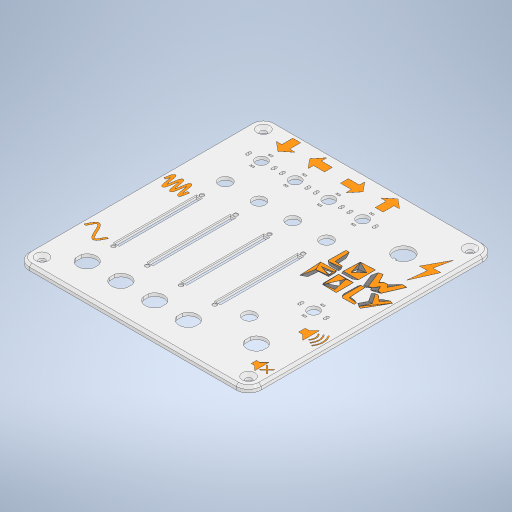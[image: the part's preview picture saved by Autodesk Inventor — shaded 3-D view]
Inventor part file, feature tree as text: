
AUTODESK INVENTOR PART (.ipt)
format: ipt  version: 2024.1 (Build 281209000, 209)  size: 8,079,360 bytes
history: native  units: mm
features: projected_geometry x59, sketch x58, extrude x57, fillet x24, other x13, chamfer x10, plane x2, pattern_linear x2
ambient origin geometry x8: Origin, YZ Plane, XZ Plane, XY Plane, X Axis, Y Axis, Z Axis, Center Point
bodies: Solid12 (feature_tree)
feature tree (225):
  other  "items"
  other  "Blocks"
  extrude  "Extrusion1"  Depth=9.5mm
  extrude  "Extrusion2"  Depth=9.5mm
  extrude  "Extrusion3"  Depth=12.0mm
  extrude  "Extrusion4"  Depth=12.0mm
  extrude  "Extrusion5"  Depth=3.3mm
  extrude  "Extrusion6"  Depth=4.0mm
  extrude  "Extrusion7"  Depth=3.3mm
  extrude  "Extrusion8"  Depth=3.3mm
  extrude  "Extrusion9"  Depth=3.3mm
  extrude  "Extrusion31"  Depth=4.3mm TaperAngle=0.0deg
  fillet  "Fillet1"  Radius=1.76mm
  extrude  "Extrusion10"  Depth=0.57mm
  plane  "Work Plane1"
  extrude  "Extrusion11"  Depth=4.96mm
  extrude  "Extrusion12"  Depth=1.22mm
  chamfer  "Chamfer1"  Distance=15.0mm
  extrude  "Extrusion13"  Depth=4.96mm
  fillet  "Fillet3"  Radius=0.49mm
  extrude  "Extrusion14"  Depth=5.0mm TaperAngle=0.0deg
  fillet  "Fillet4"  Radius=1.6mm
  extrude  "Extrusion15"  Depth=56.35mm
  extrude  "Extrusion16"  Depth=5.0mm TaperAngle=0.0deg
  extrude  "Extrusion17"  Depth=15.2mm
  extrude  "Extrusion21"  Depth=30.0mm
  extrude  "Extrusion30"  Depth=30.0mm
  fillet  "Fillet5"  Radius=10.35mm
  extrude  "Extrusion18"  Depth=1.2mm
  extrude  "Extrusion19"  Depth=7.5mm
  extrude  "Extrusion20"  Depth=5.9mm
  fillet  "Fillet6"  Radius=12.0mm
  extrude  "Extrusion22"  Depth=7.65mm
  extrude  "faceplate-extrude"  Depth=0.74mm
  fillet  "Fillet7"  Radius=9.2mm
  extrude  "Extrusion24"  Depth=4.0mm
  chamfer  "Chamfer2"  Distance=12.3mm
  chamfer  "Chamfer3"  Distance=2.0mm Angle=45.0deg
  sketch  "Sketch25"  dims[d64=0.5mm d65=7.65mm]
  extrude  "knob-extrude"  Depth=5.48mm TaperAngle=0.0deg
  extrude  "Extrusion26"  Depth=12.06mm
  extrude  "Extrusion27"  Depth=5.0mm
  chamfer  "Chamfer4"  Distance=12.3mm
  chamfer  "Chamfer5"  Distance=10.0mm
  extrude  "Extrusion28"  Depth=5.9mm
  fillet  "Fillet8"  Radius=10.0mm
  chamfer  "Chamfer6"  Distance=6.2mm
  fillet  "Fillet9"  Radius=16.0mm
  extrude  "Extrusion29"  Depth=14.5mm
  fillet  "Fillet10"  Radius=8.0mm
  chamfer  "Chamfer7"  Distance=28.0mm
  fillet  "Fillet11"  Radius=4.8mm
  chamfer  "Chamfer8"  Distance=17.15mm
  chamfer  "Chamfer9"  Distance=26.0mm
  extrude  "Extrusion32"  Depth=0.2mm
  extrude  "Extrusion33"  Depth=0.2mm
  fillet  "Fillet12"  Radius=2.87mm
  chamfer  "Chamfer10"  Distance=1.2mm
  extrude  "Extrusion34"  Depth=0.2mm
  extrude  "bracing"  Depth=0.2mm
  extrude  "Extrusion36"  Depth=0.2mm
  extrude  "graphics-controls"  Depth=0.2mm
  fillet  "Fillet13"  Radius=7.5mm
  fillet  "Fillet14"  Radius=7.5mm
  extrude  "waves"  Depth=0.2mm
  fillet  "Fillet15"  Radius=7.5mm
  fillet  "Fillet16"  Radius=7.5mm
  extrude  "logo"  Depth=0.2mm TaperAngle=0.0deg
  fillet  "Fillet17"  Radius=1.7mm
  extrude  "Extrusion41"  Depth=0.2mm
  extrude  "Extrusion42"  Depth=0.2mm
  extrude  "Extrusion43"  Depth=0.2mm TaperAngle=0.0deg
  extrude  "Extrusion44"  Depth=0.2mm
  fillet  "Fillet18"  Radius=0.2mm
  fillet  "Fillet19"  Radius=0.2mm
  fillet  "Fillet21"  Radius=0.8mm
  extrude  "Extrusion45"  Depth=0.2mm
  extrude  "Extrusion46"  Depth=0.2mm
  extrude  "Extrusion47"  Depth=0.2mm
  fillet  "Fillet20"  Radius=0.3mm
  extrude  "Extrusion48"  Depth=0.2mm
  fillet  "Fillet22"  Radius=0.1mm
  fillet  "Fillet23"  Radius=2.0mm
  plane  "Work Plane2"
  extrude  "Extrusion49"  Depth=0.2mm
  pattern_linear  "Rectangular Pattern1"  Spacing1=8.0mm  [1 undecoded]
  extrude  "Extrusion50"  Depth=0.2mm
  extrude  "Extrusion51"  TaperAngle=0.0deg  [1 undecoded]
  fillet  "Fillet24"  Radius=2.0mm
  extrude  "6.35-jack-hole"  Depth=0.2mm TaperAngle=45.0deg
  extrude  "Extrusion53"  Depth=0.2mm
  extrude  "Extrusion54"  Depth=0.2mm
  extrude  "Extrusion55"  Depth=0.2mm
  fillet  "Fillet25"  Radius=4.12mm
  extrude  "Extrusion56"  Depth=0.2mm
  extrude  "Extrusion57"  Depth=0.2mm
  extrude  "Extrusion58"  Depth=0.2mm TaperAngle=0.0deg
  pattern_linear  "Rectangular Pattern2"  Spacing1=6.5mm  [1 undecoded]
  sketch  "Sketch1"  dims[d0=60.0mm d1=9.5mm]
  sketch  "Sketch2"  dims[d2=9.5mm d3=9.5mm]
  sketch  "Sketch3"  dims[d4=9.5mm d5=12.0mm]
  sketch  "Sketch4"  dims[d6=12.0mm d7=12.0mm]
  projected_geometry  "Projected Loop1"
  sketch  "Sketch5"  dims[d8=6.0mm d9=0.0mm d10=3.3mm]
  projected_geometry  "Projected Loop2"
  projected_geometry  "Projected Loop3"
  projected_geometry  "Projected Loop4"
  sketch  "Sketch6"  dims[d11=3.3mm d12=4.0mm]
  sketch  "Sketch7"  dims[d13=4.0mm d14=3.3mm]
  sketch  "Sketch8"  dims[d15=3.3mm d16=3.3mm]
  sketch  "Sketch9"  dims[d17=3.3mm d18=3.3mm]
  projected_geometry  "Projected Loop5"
  sketch  "Sketch10"  dims[d19=3.3mm d20=4.3mm d21=0.0mm d22=1.76mm]
  projected_geometry  "Projected Loop6"
  sketch  "Sketch11"  dims[d24=2.9mm d25=0.57mm]
  projected_geometry  "Projected Loop7"
  sketch  "Sketch12"  dims[d26=1.97mm d27=4.96mm]
  sketch  "Sketch13"  dims[d28=1.495mm d29=1.22mm]
  sketch  "Sketch14"  dims[d30=0.27mm d31=15.0mm d32=0.0mm]
  sketch  "Sketch15"  dims[d33=3.98mm d34=4.96mm d35=0.49mm]
  sketch  "Sketch16"  dims[d36=5.0mm d37=0.0mm d38=5.0mm d39=0.0mm d40=1.6mm]
  sketch  "Sketch17"  dims[d41=1.825mm d42=56.35mm]
  projected_geometry  "Projected Loop8"
  sketch  "Sketch18"  dims[d43=1.825mm d44=5.0mm d45=0.0mm]
  sketch  "Sketch19"  dims[d46=19.0mm d47=15.2mm]
  projected_geometry  "Projected Loop9"
  sketch  "Sketch20"  dims[d48=16.4mm d49=30.0mm]
  projected_geometry  "Projected Loop10"
  sketch  "Sketch21"  dims[d50=30.0mm d51=30.0mm d53=10.35mm d54=0.0mm]
  projected_geometry  "Projected Loop11"
  projected_geometry  "Projected Loop12"
  projected_geometry  "Projected Loop13"
  projected_geometry  "Projected Loop14"
  projected_geometry  "Projected Loop15"
  projected_geometry  "Projected Loop16"
  projected_geometry  "Projected Loop17"
  projected_geometry  "Projected Loop18"
  projected_geometry  "Projected Loop19"
  projected_geometry  "Projected Loop20"
  projected_geometry  "Projected Loop21"
  sketch  "Sketch22"  dims[d55=6.8mm d56=1.2mm]
  projected_geometry  "Projected Loop22"
  projected_geometry  "Projected Loop23"
  projected_geometry  "Projected Loop24"
  projected_geometry  "Projected Loop25"
  projected_geometry  "Projected Loop26"
  sketch  "Sketch23"  dims[d57=2.87mm d58=7.5mm]
  other  "faceplate"
  sketch  "Sketch24"  dims[d59=4.5mm d60=0.0mm d61=5.9mm d62=12.0mm d63=0.0mm]
  sketch  "Sketch26"  dims[d67=13.0mm d68=0.74mm d69=9.2mm d70=0.0mm]
  projected_geometry  "Projected Loop27"
  other  "slider-knob"
  sketch  "Sketch27"  dims[d71=9.1mm d72=4.0mm d73=-1.745329mm]
  projected_geometry  "Projected Loop28"
  sketch  "Sketch28"  dims[d74=2.0mm]
  projected_geometry  "Projected Loop29"
  sketch  "Sketch29"  dims[d75=11.64mm]
  projected_geometry  "Projected Loop30"
  sketch  "Sketch30"  dims[d76=15.0mm]
  sketch  "Sketch31"  dims[d77=20.0mm d78=12.3mm d79=0.0mm d80=2.0mm d81=2.0mm d82=45.0deg]
  sketch  "Sketch32"  dims[d83=17.62mm d84=5.48mm d85=0.0mm]
  projected_geometry  "Projected Loop31"
  projected_geometry  "Projected Loop32"
  projected_geometry  "Projected Loop33"
  projected_geometry  "Projected Loop34"
  projected_geometry  "Projected Loop35"
  projected_geometry  "Projected Loop36"
  projected_geometry  "Projected Loop37"
  projected_geometry  "Projected Loop38"
  projected_geometry  "Projected Loop39"
  projected_geometry  "Projected Loop40"
  projected_geometry  "Projected Loop41"
  projected_geometry  "Projected Loop42"
  projected_geometry  "Projected Loop43"
  projected_geometry  "Projected Loop45"
  sketch  "Sketch33"  dims[d87=2.0mm d88=12.06mm]
  sketch  "Sketch34"  dims[d89=3.0mm d90=0.0mm d91=5.0mm]
  sketch  "Sketch35"  dims[d92=11.1mm]
  projected_geometry  "Projected Loop46"
  projected_geometry  "Projected Loop47"
  projected_geometry  "Projected Loop48"
  projected_geometry  "Projected Loop49"
  projected_geometry  "Projected Loop50"
  projected_geometry  "Projected Loop51"
  projected_geometry  "Projected Loop52"
  projected_geometry  "Projected Loop53"
  projected_geometry  "Projected Loop54"
  projected_geometry  "Projected Loop55"
  projected_geometry  "Projected Loop56"
  sketch  "Sketch36"  dims[d93=5.55mm]
  sketch  "Sketch37"  dims[d94=11.1mm]
  sketch  "Sketch38"  dims[d95=5.55mm]
  other  "2D Equation Curve1"
  sketch  "Sketch40"  dims[d96=11.1mm]
  other  "2D Equation Curve2"
  other  "2D Equation Curve4"
  other  "low-poly-logo"
  sketch  "Sketch42"  dims[d97=5.55mm]
  other  "000-low-poly-logo"
  sketch  "Sketch43"  dims[d98=11.1mm]
  projected_geometry  "Projected Loop57"
  other  "case-body"
  sketch  "Sketch44"  dims[d99=5.55mm]
  projected_geometry  "Projected Loop58"
  sketch  "Sketch45"  dims[d100=11.1mm]
  projected_geometry  "Projected Loop59"
  projected_geometry  "Projected Loop60"
  sketch  "Sketch46"  dims[d101=5.55mm]
  sketch  "Sketch47"  dims[d102=10.7mm]
  other  "circuit-boards"
  sketch  "Sketch48"  dims[d103=10.7mm]
  sketch  "Sketch49"  dims[d104=15.2mm]
  sketch  "Sketch50"  dims[d105=15.2mm]
  sketch  "Sketch51"  dims[d108=23.0mm]
  sketch  "Sketch52"  dims[d109=17.0mm d110=12.3mm d111=0.0mm]
  sketch  "Sketch53"  dims[d112=6.8mm]
  sketch  "Sketch54"  dims[d113=6.8mm d114=10.0mm d115=0.0mm]
  sketch  "Sketch55"  dims[d116=5.9mm d117=5.9mm d118=10.0mm d119=0.0mm]
  other  "jacks"
  sketch  "Sketch56"  dims[d120=0.2mm]
  sketch  "Sketch57"  dims[d121=11.9mm d122=6.2mm d123=0.0mm d124=16.0mm]
  sketch  "Sketch58"  dims[d125=29.0mm d126=14.5mm d127=8.0mm d128=28.0mm d129=0.0mm d130=4.8mm d131=17.15mm d132=0.523599mm]
  sketch  "Sketch59"  dims[d133=2.0mm]
  sketch  "Sketch60"  dims[d134=20.0mm d135=26.0mm d136=16.0mm d138=1.2mm d139=2.87mm d140=1.2mm d141=1.2mm d142=1.2mm d143=1.2mm d144=2.87mm d145=7.5mm d146=7.5mm d147=7.5mm d148=7.5mm d149=7.5mm d150=17.15mm d151=0.0mm d152=1.7mm d153=5.2mm d154=0.85mm d155=10.0mm d156=0.0mm d157=20.0mm d158=0.2mm d159=0.2mm d160=0.8mm d161=0.1mm d162=0.1mm d163=0.2mm d164=0.3mm d165=0.25mm d166=0.1mm d167=2.0mm d168=0.0mm d169=0.2mm d170=8.0mm d171=4.0mm d172=0.0mm d173=0.0mm d174=2.0mm d175=2.0mm d176=45.0deg d177=0.2mm d178=2.0mm d179=45.0deg d180=10.0mm d181=22.0mm d182=1.76mm d183=4.12mm d184=3.98mm d185=9.01mm d186=10.0mm d187=0.0mm d188=6.5mm d189=0.0mm d190=2.5mm d191=0.0mm d192=4.0mm d193=2.0mm d194=45.0deg d195=2.5mm d196=9.0mm d197=45.0deg d198=0.0mm d199=0.0mm d200=1.0mm d201=2.5mm d202=9.0mm d203=45.0deg d204=2.0mm d205=0.9mm d206=1.2mm d207=1.8mm d208=1.3mm d209=2.0mm d210=1.5mm d211=1.0mm d212=0.0mm d213=0.0mm d214=0.4mm d215=3.341737mm d216=2.5mm d217=9.0mm d218=45.0deg d219=0.5mm d221=7.5mm d222=7.5mm d223=7.5mm d224=7.5mm d225=1.2mm d226=1.2mm d227=1.2mm d228=1.2mm d229=5.5mm d230=1.9mm d231=0.77mm d232=1.9mm d233=0.77mm d234=1.9mm d235=0.77mm d236=1.9mm d237=0.77mm d238=1.9mm d239=0.77mm d240=1.9mm d241=0.77mm d242=1.9mm d243=0.77mm d244=1.9mm d245=0.77mm d246=5.5mm d247=1.4mm d248=0.0mm d249=1.2mm d253=1.2mm d255=7.5mm d256=2.87mm d257=1.9mm d258=0.77mm d259=1.9mm d260=0.77mm d261=11.0mm d262=5.5mm d263=1.4mm d264=0.0mm d265=0.2mm d266=0.5mm d267=2.0mm d268=45.0deg d269=1.5mm d270=2.0mm d271=45.0deg d273=1.5mm d274=0.5mm d275=0.0mm d276=25.0mm d277=0.4mm d278=0.0mm d279=2.0mm d280=0.4mm d281=2.0mm d282=45.0deg d283=12.0mm d284=1.5mm d285=0.0mm d286=1.5mm d287=0.0mm d288=21.0mm d289=1.5mm d290=0.0mm d304=7.0mm d314=5.0mm d315=5.0mm d316=12.0mm d317=2.0mm d318=12.0mm d319=7.0mm d320=7.0mm d321=5.0mm d322=5.0mm d323=5.0mm d324=5.0mm d325=7.0mm d326=5.0mm d327=5.0mm d328=12.0mm d329=12.0mm d330=3.0mm d331=4.2mm d332=3.36mm d333=2.52mm d334=3.36mm d335=10.92mm d336=0.672mm d337=2.94mm d338=2.94mm d339=4.116mm d340=4.116mm d341=5.208mm d342=0.672mm d343=0.672mm d344=1.68mm d345=1.68mm d346=1.68mm d347=3.36mm d348=2.94mm d349=2.1mm d350=2.94mm d351=13.0mm d363=45.0deg d364=90.0deg d365=3.36mm d366=0.756mm d367=0.756mm d368=2.1mm d369=2.1mm d370=0.0mm d371=10.0mm d372=0.05mm d373=0.0mm d374=0.1mm d375=0.05mm d376=0.0mm d377=10.0mm d380=0.0mm d381=3600.0mm d390=0.0mm d391=10800.0mm d394=0.0mm d395=10800.0mm d396=1.5mm d397=1.0mm d398=3.0mm d400=0.0mm d401=3600.0mm d402=1.5mm d403=3.0mm d404=1.0mm d405=0.05mm d406=0.0mm d407=1.0mm d408=0.15mm d422=5.208mm d426=0.05mm d427=0.0mm d428=60.0mm d429=32.0mm d430=0.1mm d431=0.1mm d432=0.1mm d435=0.1mm d437=30.0mm d438=0.0mm d439=0.4mm d440=2.0mm d441=2.0mm d442=0.0mm d443=2.0mm d444=0.0mm d445=43.0mm d446=55.0mm d447=3.0mm d448=3.0mm d449=6.0mm d450=0.0mm d451=2.0mm d452=5.0mm d453=43.0mm d454=55.0mm d455=3.0mm d456=3.0mm d457=3.0mm d458=4.0mm d459=0.0mm d460=10.1mm d461=19.1mm d462=11.2mm d463=23.0mm d464=7.0mm d465=0.0mm d466=16.4mm d469=32.0mm d470=0.0mm d471=1.0mm d473=4.12mm d474=5.5mm d475=1.0mm d476=0.5mm d477=3.2mm d478=5.0mm d479=3.0mm d481=5.0mm d482=5.0mm d483=5.0mm d484=3.0mm d485=4.0mm d486=4.0mm d487=5.0mm d488=8.0mm d489=44.0mm d490=0.0mm d491=0.0mm d492=260.0mm d493=3.0mm d494=30.0mm d495=11.5mm d496=11.5mm d497=3.0mm d498=0.0mm d499=30.0mm d501=11.0mm d502=5.0mm d503=4.0mm d504=6.0mm d505=0.0mm d506=4.999995mm d507=5.0mm d508=1.5mm d509=1.499992mm d510=3.0mm d511=1.5mm d512=5.0mm d513=6.0mm d514=28.0mm d515=0.0mm d516=0.0mm d517=200.0mm d518=11.0mm d519=20.0mm d520=8.0mm d521=22.0mm d522=6.0mm d523=0.0mm d524=10.83mm d525=8.5mm d526=0.0mm d527=6.5mm d528=20.1mm d529=10.05mm d530=7.9mm d531=14.8mm d532=26.0mm d533=0.0mm d534=0.4mm d535=0.4mm d536=1.3mm d537=1.3mm d538=1.3mm d539=3.4mm d540=2.0mm d541=2.0mm d542=5.05mm d543=5.05mm d544=4.5mm d545=0.0mm d546=0.6mm d547=24.0mm d548=14.0mm d549=11.5mm d550=0.0mm d551=0.0mm d552=18.0mm d553=22.0mm d554=0.0mm d555=4.0mm d556=3.0mm d557=22.0mm d558=0.0mm d559=20.0mm d561=131.6mm d562=20.0mm d564=141.0mm]
  other  "000-low-poly-logo:1"
note: 3 required parameter values undecoded (feature->parameter linkage not recoverable at this tier; creation-order binding heuristic only, values carry confidence <= 0.55)
